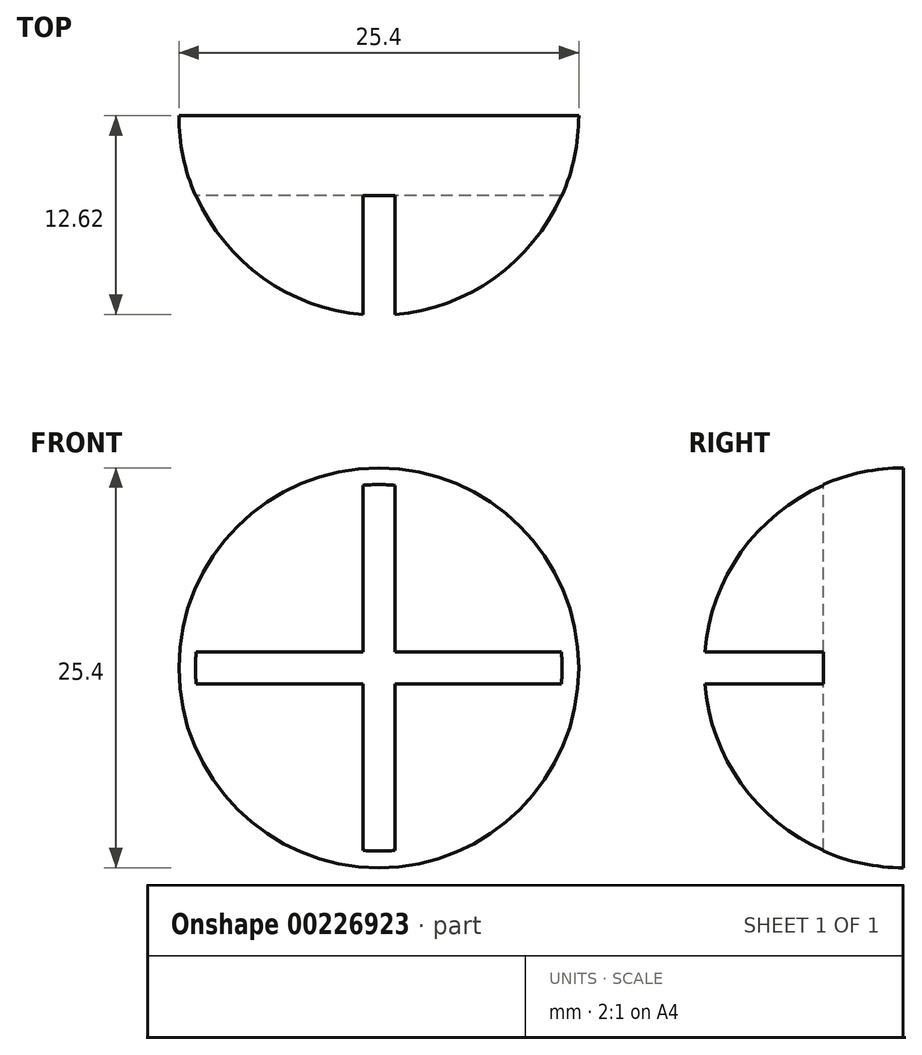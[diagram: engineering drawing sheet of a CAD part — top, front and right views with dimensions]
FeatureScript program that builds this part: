
annotation { "Feature Type Name" : "Feature", "Feature Type Description" : "" }
export const myFeature = defineFeature(function(context is Context, id is Id, definition is map)
    precondition{}
    {
        {
            var Q0;
            Q0=qCreatedBy(makeId("Front.planeOp"),FACE);
            var sketch = newSketch(context, id + "F0", { "sketchPlane" : qUnion([Q0])});
            skLineSegment(sketch, "E0", {"start": v(-12.7, 0) * mm, "end": v(12.7, 0) * mm});
            skArc(sketch, "E1", {"start": v(12.7, 0) * mm, "mid": v(0, 12.7) * mm, "end": v(-12.7, 0) * mm});
            skSolve(sketch);
        }
        {
            var Q0;
            Q0=makeQuery(id+"F0.imprint","IMPRINT",FACE,{"disambiguationData":[TD([[makeQuery(id+"F0.imprint","IMPRINT",EDGE,{"derivedFrom":sQuery(id+"F0.wireOp",EDGE,"E0")}),1.0]])]});
            var Q1;
            Q1=sQuery(id+"F0.wireOp",EDGE,"E0");
            revolve(context, id + "F1", {"entities" : qUnion([Q0]), "axis" : qUnion([Q1]), "revolveType" : RevolveType.ONE_DIRECTION, "angle" : 180 * degree});
        }
        {
            var Q0;
            Q0=qCreatedBy(makeId("Right.planeOp"),FACE);
            var sketch = newSketch(context, id + "F2", { "sketchPlane" : qUnion([Q0])});
            skLineSegment(sketch, "E2.bottom", {"start": v(-30.48, 1.02) * mm, "end": v(-5.08, 1.02) * mm});
            skLineSegment(sketch, "E2.top", {"start": v(-30.48, -1.02) * mm, "end": v(-5.08, -1.02) * mm});
            skLineSegment(sketch, "E2.left", {"start": v(-30.48, 1.02) * mm, "end": v(-30.48, -1.02) * mm});
            skLineSegment(sketch, "E2.right", {"start": v(-5.08, 1.02) * mm, "end": v(-5.08, -1.02) * mm});
            skSolve(sketch);
        }
        {
            var Q0;
            Q0=makeQuery(id+"F2.imprint","IMPRINT",FACE,{"disambiguationData":[TD([[makeQuery(id+"F2.imprint","IMPRINT",EDGE,{"derivedFrom":sQuery(id+"F2.wireOp",EDGE,"E2.bottom")}),-1.0]])]});
            extrude(context, id + "F3", {"entities" : qUnion([Q0]), "operationType" : NewBodyOperationType.REMOVE, "endBound" : BoundingType.SYMMETRIC, "depth" : 25.4 * mm});
        }
        {
            var Q0;
            Q0=qCreatedBy(makeId("Top.planeOp"),FACE);
            var sketch = newSketch(context, id + "F4", { "sketchPlane" : qUnion([Q0])});
            skLineSegment(sketch, "E3.bottom", {"start": v(-1.02, -5.08) * mm, "end": v(1.02, -5.08) * mm});
            skLineSegment(sketch, "E3.top", {"start": v(-1.02, -30.48) * mm, "end": v(1.02, -30.48) * mm});
            skLineSegment(sketch, "E3.left", {"start": v(-1.02, -5.08) * mm, "end": v(-1.02, -30.48) * mm});
            skLineSegment(sketch, "E3.right", {"start": v(1.02, -5.08) * mm, "end": v(1.02, -30.48) * mm});
            skSolve(sketch);
        }
        {
            var Q0;
            Q0=makeQuery(id+"F4.imprint","IMPRINT",FACE,{"disambiguationData":[TD([[makeQuery(id+"F4.imprint","IMPRINT",EDGE,{"derivedFrom":sQuery(id+"F4.wireOp",EDGE,"E3.bottom")}),-1.0]])]});
            extrude(context, id + "F5", {"entities" : qUnion([Q0]), "operationType" : NewBodyOperationType.REMOVE, "endBound" : BoundingType.SYMMETRIC, "oppositeDirection" : true, "depth" : 25.4 * mm});
        }
    });
